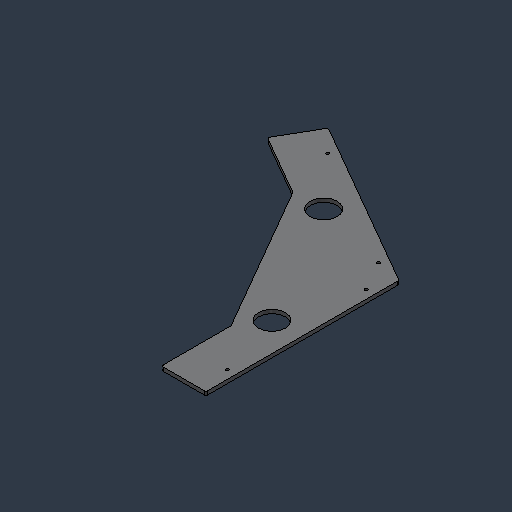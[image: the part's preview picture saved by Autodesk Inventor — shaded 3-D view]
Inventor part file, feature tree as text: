
AUTODESK INVENTOR PART (.ipt)
format: ipt  version: 2024.3 (Build 283343000, 343)  size: 92,672 bytes
history: native  units: mm (DEFAULTED — no unit token found)
features: fillet x1
ambient origin geometry x8: Origin, YZ Plane, XZ Plane, XY Plane, X Axis, Y Axis, Z Axis, Center Point
bodies: Solid1 (feature_tree)
feature tree (1):
  fillet  "Fillet1"  [1 undecoded]
note: 1 required parameter value undecoded (feature->parameter linkage not recoverable at this tier; creation-order binding heuristic only, values carry confidence <= 0.55)
